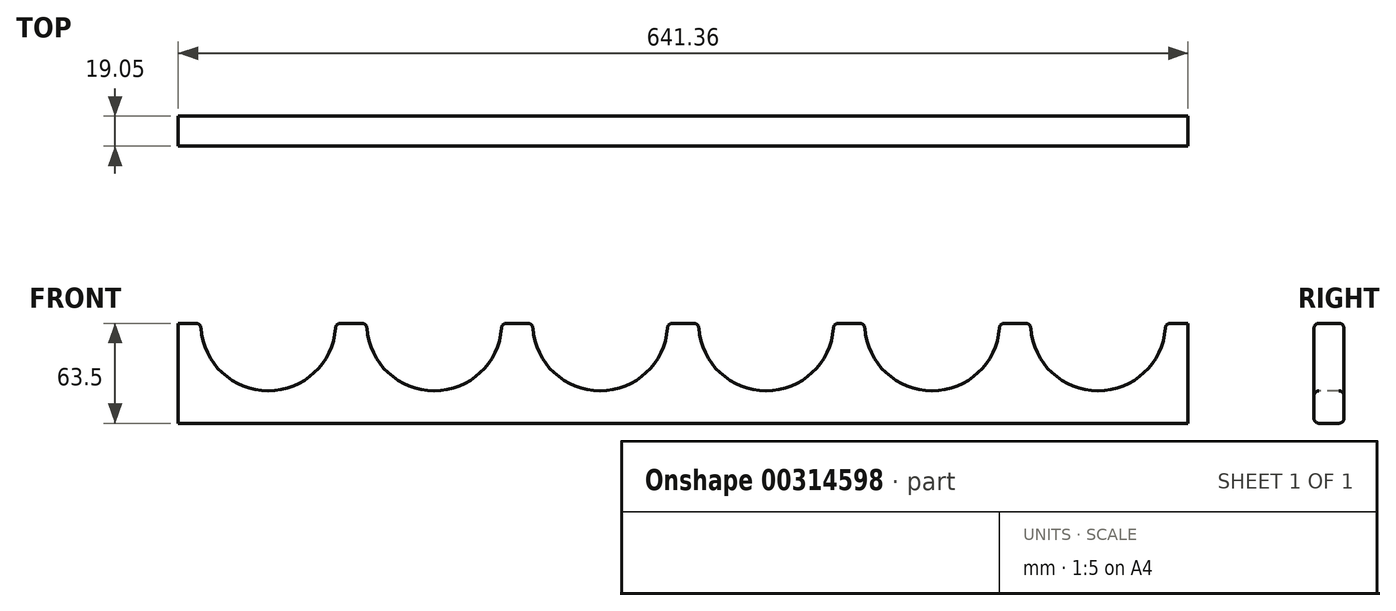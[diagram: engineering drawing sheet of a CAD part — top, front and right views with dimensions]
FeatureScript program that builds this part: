
annotation { "Feature Type Name" : "Feature", "Feature Type Description" : "" }
export const myFeature = defineFeature(function(context is Context, id is Id, definition is map)
    precondition{}
    {
        {
            var Q0;
            Q0=qCreatedBy(makeId("Front.planeOp"),FACE);
            var sketch = newSketch(context, id + "F0", { "sketchPlane" : qUnion([Q0])});
            skLineSegment(sketch, "E0.top", {"start": v(-320.68, -31.75) * mm, "end": v(320.68, -31.75) * mm});
            skLineSegment(sketch, "E0.left", {"start": v(-320.68, 31.75) * mm, "end": v(-320.68, -31.75) * mm});
            skLineSegment(sketch, "E0.right", {"start": v(320.68, 31.75) * mm, "end": v(320.68, -31.75) * mm});
            skLineSegment(sketch, "E1", {"start": v(-320.68, -31.75) * mm, "end": v(320.67, 31.75) * mm, "construction": true});
            skLineSegment(sketch, "E2", {"start": v(-320.68, 31.75) * mm, "end": v(-263.53, 31.75) * mm});
            skLineSegment(sketch, "E3", {"start": v(-263.53, 31.75) * mm, "end": v(-158.12, 31.75) * mm});
            skLineSegment(sketch, "E4", {"start": v(263.53, 31.75) * mm, "end": v(320.68, 31.75) * mm});
            skLineSegment(sketch, "E5", {"start": v(-158.12, 31.75) * mm, "end": v(-52.7, 31.75) * mm});
            skLineSegment(sketch, "E6", {"start": v(-52.7, 31.75) * mm, "end": v(52.7, 31.75) * mm});
            skLineSegment(sketch, "E7", {"start": v(158.12, 31.75) * mm, "end": v(263.53, 31.75) * mm});
            skLineSegment(sketch, "E8", {"start": v(52.7, 31.75) * mm, "end": v(158.12, 31.75) * mm});
            skCircle(sketch, "E9", {"center": v(-263.53, 31.75) * mm, "radius": 42.86 * mm});
            skCircle(sketch, "E10", {"center": v(-158.11, 31.75) * mm, "radius": 42.86 * mm});
            skCircle(sketch, "E11", {"center": v(-52.7, 31.75) * mm, "radius": 42.86 * mm});
            skCircle(sketch, "E12", {"center": v(52.7, 31.75) * mm, "radius": 42.86 * mm});
            skCircle(sketch, "E13", {"center": v(158.12, 31.75) * mm, "radius": 42.86 * mm});
            skCircle(sketch, "E14", {"center": v(263.53, 31.75) * mm, "radius": 42.86 * mm});
            skSolve(sketch);
        }
        {
            var Q0;
            Q0=makeQuery(id+"F0.imprint","IMPRINT",FACE,{"disambiguationData":[TD([[makeQuery(id+"F0.imprint","IMPRINT",EDGE,{"derivedFrom":sQuery(id+"F0.wireOp",EDGE,"E0.top")}),1.0]])]});
            extrude(context, id + "F1", {"entities" : qUnion([Q0]), "oppositeDirection" : true, "depth" : 19.05 * mm});
        }
        {
            var Q0;
            Q0=makeQuery(id+"F1.opExtrude","CAP_EDGE",EDGE,{"disambiguationData":[OSD([sQuery(id+"F0.wireOp",EDGE,"E2")])],"isStart":true});
            var Q1;
            Q1=makeQuery(id+"F1.opExtrude","SWEPT_EDGE",EDGE,{"disambiguationData":[OSD([sQuery(id+"F0.wireOp",EDGE,"E2"),sQuery(id+"F0.wireOp",EDGE,"E9")])]});
            var Q2;
            Q2=makeQuery(id+"F1.opExtrude","CAP_EDGE",EDGE,{"disambiguationData":[OSD([sQuery(id+"F0.wireOp",EDGE,"E2")])],"isStart":false});
            var Q3;
            Q3=makeQuery(id+"F1.opExtrude","CAP_EDGE",EDGE,{"disambiguationData":[OSD([sQuery(id+"F0.wireOp",EDGE,"E9")])],"isStart":false});
            var Q4;
            Q4=makeQuery(id+"F1.opExtrude","CAP_EDGE",EDGE,{"disambiguationData":[OSD([sQuery(id+"F0.wireOp",EDGE,"E9")])],"isStart":true});
            var Q5;
            Q5=makeQuery(id+"F1.opExtrude","SWEPT_EDGE",EDGE,{"disambiguationData":[OSD([sQuery(id+"F0.wireOp",EDGE,"E3"),sQuery(id+"F0.wireOp",EDGE,"E9")])]});
            var Q6;
            Q6=makeQuery(id+"F1.opExtrude","CAP_EDGE",EDGE,{"disambiguationData":[OSD([sQuery(id+"F0.wireOp",EDGE,"E3")])],"isStart":false});
            var Q7;
            Q7=makeQuery(id+"F1.opExtrude","CAP_EDGE",EDGE,{"disambiguationData":[OSD([sQuery(id+"F0.wireOp",EDGE,"E3")])],"isStart":true});
            var Q8;
            Q8=makeQuery(id+"F1.opExtrude","SWEPT_EDGE",EDGE,{"disambiguationData":[OSD([sQuery(id+"F0.wireOp",EDGE,"E3"),sQuery(id+"F0.wireOp",EDGE,"E10")])]});
            var Q9;
            Q9=makeQuery(id+"F1.opExtrude","CAP_EDGE",EDGE,{"disambiguationData":[OSD([sQuery(id+"F0.wireOp",EDGE,"E10")])],"isStart":false});
            var Q10;
            Q10=makeQuery(id+"F1.opExtrude","CAP_EDGE",EDGE,{"disambiguationData":[OSD([sQuery(id+"F0.wireOp",EDGE,"E10")])],"isStart":true});
            var Q11;
            Q11=makeQuery(id+"F1.opExtrude","SWEPT_EDGE",EDGE,{"disambiguationData":[OSD([sQuery(id+"F0.wireOp",EDGE,"E5"),sQuery(id+"F0.wireOp",EDGE,"E10")])]});
            var Q12;
            Q12=makeQuery(id+"F1.opExtrude","CAP_EDGE",EDGE,{"disambiguationData":[OSD([sQuery(id+"F0.wireOp",EDGE,"E5")])],"isStart":true});
            var Q13;
            Q13=makeQuery(id+"F1.opExtrude","CAP_EDGE",EDGE,{"disambiguationData":[OSD([sQuery(id+"F0.wireOp",EDGE,"E5")])],"isStart":false});
            var Q14;
            Q14=makeQuery(id+"F1.opExtrude","SWEPT_EDGE",EDGE,{"disambiguationData":[OSD([sQuery(id+"F0.wireOp",EDGE,"E5"),sQuery(id+"F0.wireOp",EDGE,"E11")])]});
            var Q15;
            Q15=makeQuery(id+"F1.opExtrude","CAP_EDGE",EDGE,{"disambiguationData":[OSD([sQuery(id+"F0.wireOp",EDGE,"E11")])],"isStart":false});
            var Q16;
            Q16=makeQuery(id+"F1.opExtrude","CAP_EDGE",EDGE,{"disambiguationData":[OSD([sQuery(id+"F0.wireOp",EDGE,"E11")])],"isStart":true});
            var Q17;
            Q17=makeQuery(id+"F1.opExtrude","SWEPT_EDGE",EDGE,{"disambiguationData":[OSD([sQuery(id+"F0.wireOp",EDGE,"E6"),sQuery(id+"F0.wireOp",EDGE,"E11")])]});
            var Q18;
            Q18=makeQuery(id+"F1.opExtrude","SWEPT_FACE",FACE,{"disambiguationData":[OSD([sQuery(id+"F0.wireOp",EDGE,"E6")])]});
            var Q19;
            Q19=makeQuery(id+"F1.opExtrude","CAP_EDGE",EDGE,{"disambiguationData":[OSD([sQuery(id+"F0.wireOp",EDGE,"E6")])],"isStart":true});
            var Q20;
            Q20=makeQuery(id+"F1.opExtrude","CAP_EDGE",EDGE,{"disambiguationData":[OSD([sQuery(id+"F0.wireOp",EDGE,"E12")])],"isStart":true});
            var Q21;
            Q21=makeQuery(id+"F1.opExtrude","CAP_EDGE",EDGE,{"disambiguationData":[OSD([sQuery(id+"F0.wireOp",EDGE,"E12")])],"isStart":false});
            var Q22;
            Q22=makeQuery(id+"F1.opExtrude","SWEPT_FACE",FACE,{"disambiguationData":[OSD([sQuery(id+"F0.wireOp",EDGE,"E8")])]});
            var Q23;
            Q23=makeQuery(id+"F1.opExtrude","SWEPT_FACE",FACE,{"disambiguationData":[OSD([sQuery(id+"F0.wireOp",EDGE,"E13")])]});
            var Q24;
            Q24=makeQuery(id+"F1.opExtrude","SWEPT_FACE",FACE,{"disambiguationData":[OSD([sQuery(id+"F0.wireOp",EDGE,"E7")])]});
            var Q25;
            Q25=makeQuery(id+"F1.opExtrude","SWEPT_FACE",FACE,{"disambiguationData":[OSD([sQuery(id+"F0.wireOp",EDGE,"E14")])]});
            var Q26;
            Q26=makeQuery(id+"F1.opExtrude","CAP_EDGE",EDGE,{"disambiguationData":[OSD([sQuery(id+"F0.wireOp",EDGE,"E4")])],"isStart":false});
            var Q27;
            Q27=makeQuery(id+"F1.opExtrude","CAP_EDGE",EDGE,{"disambiguationData":[OSD([sQuery(id+"F0.wireOp",EDGE,"E4")])],"isStart":true});
            fillet(context, id + "F2", {"entities" : qUnion([Q0, Q1, Q2, Q3, Q4, Q5, Q6, Q7, Q8, Q9, Q10, Q11, Q12, Q13, Q14, Q15, Q16, Q17, Q18, Q19, Q20, Q21, Q22, Q23, Q24, Q25, Q26, Q27]), "radius" : 3.17 * mm, "tangentPropagation" : true, "allowEdgeOverflow" : false});
        }
        {
            var Q0;
            Q0=makeQuery(id+"F1.opExtrude","CAP_EDGE",EDGE,{"disambiguationData":[OSD([sQuery(id+"F0.wireOp",EDGE,"E0.top")])],"isStart":true});
            var Q1;
            Q1=makeQuery(id+"F1.opExtrude","CAP_EDGE",EDGE,{"disambiguationData":[OSD([sQuery(id+"F0.wireOp",EDGE,"E0.top")])],"isStart":false});
            fillet(context, id + "F3", {"entities" : qUnion([Q0, Q1]), "radius" : 3.17 * mm, "tangentPropagation" : true, "allowEdgeOverflow" : false});
        }
    });
